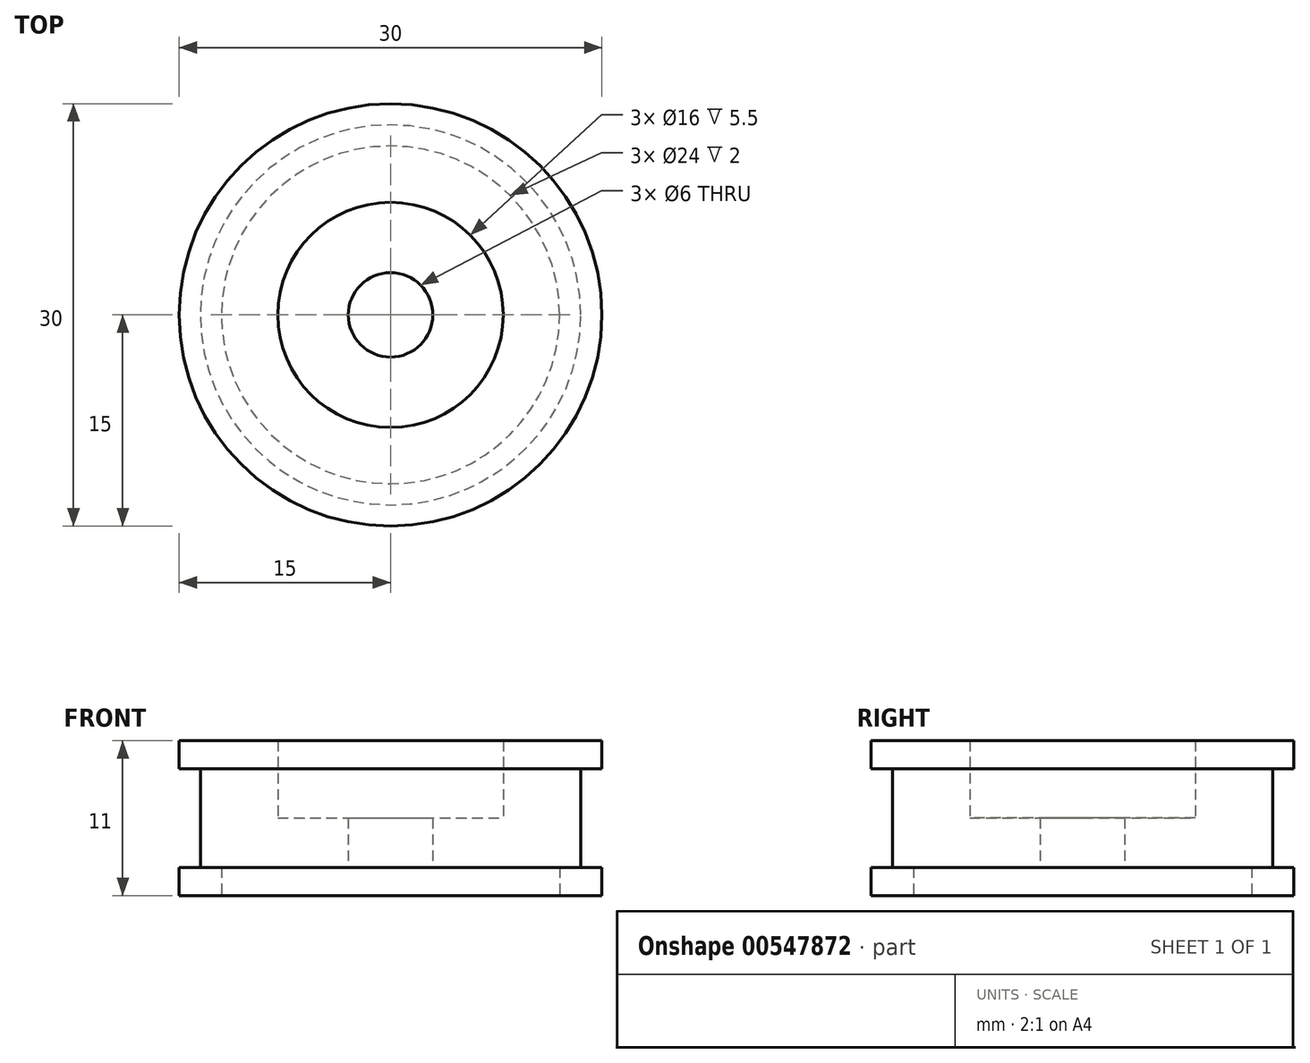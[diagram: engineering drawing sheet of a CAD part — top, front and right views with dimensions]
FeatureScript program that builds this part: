
annotation { "Feature Type Name" : "Feature", "Feature Type Description" : "" }
export const myFeature = defineFeature(function(context is Context, id is Id, definition is map)
    precondition{}
    {
        {
            var Q0;
            Q0=qCreatedBy(makeId("Front.planeOp"),FACE);
            var sketch = newSketch(context, id + "F0", { "sketchPlane" : qUnion([Q0])});
            skLineSegment(sketch, "E0", {"start": v(0, 0) * mm, "end": v(0, 4.64) * mm, "construction": true});
            skLineSegment(sketch, "E1", {"start": v(-15, 9) * mm, "end": v(-8, 9) * mm});
            skLineSegment(sketch, "E2", {"start": v(-8, 9) * mm, "end": v(-8, 3.5) * mm});
            skLineSegment(sketch, "E3", {"start": v(-8, 3.5) * mm, "end": v(-3, 3.5) * mm});
            skLineSegment(sketch, "E4", {"start": v(-3, 3.5) * mm, "end": v(-3, 0) * mm});
            skLineSegment(sketch, "E5", {"start": v(-15, -2) * mm, "end": v(-12, -2) * mm});
            skLineSegment(sketch, "E6", {"start": v(-12, -2) * mm, "end": v(-12, 0) * mm});
            skLineSegment(sketch, "E7", {"start": v(-12, 0) * mm, "end": v(-3, 0) * mm});
            skLineSegment(sketch, "E8", {"start": v(-15, 9) * mm, "end": v(-15, 7) * mm});
            skLineSegment(sketch, "E9", {"start": v(-15, 7) * mm, "end": v(-13.5, 7) * mm});
            skLineSegment(sketch, "E10", {"start": v(-13.5, 7) * mm, "end": v(-13.5, 0) * mm});
            skLineSegment(sketch, "E11", {"start": v(-13.5, 0) * mm, "end": v(-15, 0) * mm});
            skLineSegment(sketch, "E12", {"start": v(-15, 0) * mm, "end": v(-15, -2) * mm});
            skSolve(sketch);
        }
        {
            var Q0;
            Q0=makeQuery(id+"F0.imprint","IMPRINT",FACE,{"disambiguationData":[TD([[makeQuery(id+"F0.imprint","IMPRINT",EDGE,{"derivedFrom":sQuery(id+"F0.wireOp",EDGE,"E1")}),-1.0]])]});
            var Q1;
            Q1=sQuery(id+"F0.wireOp",EDGE,"E0");
            revolve(context, id + "F1", {"entities" : qUnion([Q0]), "axis" : qUnion([Q1]), "revolveType" : RevolveType.FULL});
        }
    });
